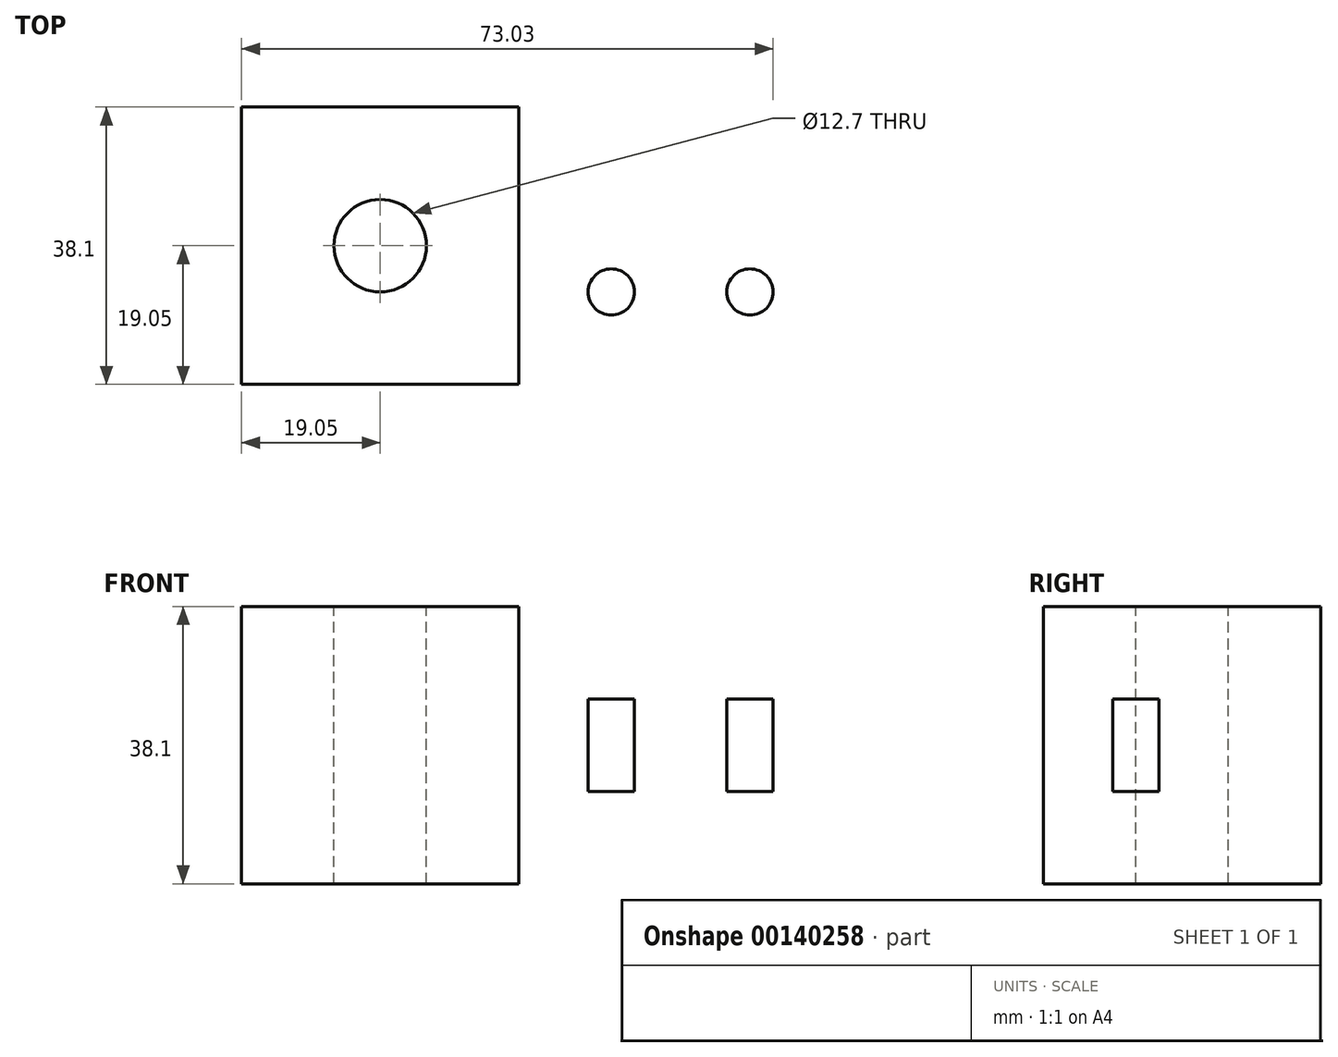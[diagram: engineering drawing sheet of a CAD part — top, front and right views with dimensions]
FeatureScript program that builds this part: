
annotation { "Feature Type Name" : "Feature", "Feature Type Description" : "" }
export const myFeature = defineFeature(function(context is Context, id is Id, definition is map)
    precondition{}
    {
        {
            var Q0;
            Q0=qCreatedBy(makeId("Front.planeOp"),FACE);
            var sketch = newSketch(context, id + "F0", { "sketchPlane" : qUnion([Q0])});
            skLineSegment(sketch, "E0", {"start": v(0, 0) * mm, "end": v(0, 38.1) * mm});
            skLineSegment(sketch, "E1", {"start": v(0, 38.1) * mm, "end": v(38.1, 38.1) * mm});
            skLineSegment(sketch, "E2", {"start": v(38.1, 38.1) * mm, "end": v(38.1, 25.4) * mm});
            skLineSegment(sketch, "E3", {"start": v(38.1, 25.4) * mm, "end": v(88.9, 25.4) * mm});
            skLineSegment(sketch, "E4", {"start": v(88.9, 25.4) * mm, "end": v(88.9, 12.7) * mm});
            skLineSegment(sketch, "E5", {"start": v(88.9, 12.7) * mm, "end": v(38.1, 12.7) * mm});
            skLineSegment(sketch, "E6", {"start": v(38.1, 12.7) * mm, "end": v(38.1, 0) * mm});
            skLineSegment(sketch, "E7", {"start": v(38.1, 0) * mm, "end": v(0, 0) * mm});
            skSolve(sketch);
        }
        {
            var Q0;
            Q0 = qSketchRegion(id + "F0", true);
            extrude(context, id + "F1", {"entities" : qUnion([Q0]), "endBound" : BoundingType.SYMMETRIC, "depth" : 38.1 * mm});
        }
        {
            var Q0;
            Q0=makeQuery(id+"F1.opExtrude","CAP_EDGE",EDGE,{"disambiguationData":[OSD([sQuery(id+"F0.wireOp",EDGE,"E4")])],"isStart":true});
            var Q1;
            Q1=makeQuery(id+"F1.opExtrude","CAP_EDGE",EDGE,{"disambiguationData":[OSD([sQuery(id+"F0.wireOp",EDGE,"E4")])],"isStart":false});
            fillet(context, id + "F2", {"entities" : qUnion([Q0, Q1]), "radius" : 19.05 * mm, "tangentPropagation" : true, "allowEdgeOverflow" : false});
        }
        {
            var Q0;
            Q0=makeQuery(id+"F1.opExtrude","SWEPT_FACE",FACE,{"disambiguationData":[OSD([sQuery(id+"F0.wireOp",EDGE,"E1")])]});
            var sketch = newSketch(context, id + "F3", { "sketchPlane" : qUnion([Q0])});
            skCircle(sketch, "E8", {"center": v(19.05, 0) * mm, "radius": 6.35 * mm});
            skPoint(sketch, "E8.centerSnap0", {"position": v(19.05, 19.05) * mm});
            skSolve(sketch);
        }
        {
            var Q0;
            Q0=makeQuery(id+"F1.opExtrude","SWEPT_FACE",FACE,{"disambiguationData":[OSD([sQuery(id+"F0.wireOp",EDGE,"E3")])]});
            var sketch = newSketch(context, id + "F4", { "sketchPlane" : qUnion([Q0])});
            skCircle(sketch, "E9", {"center": v(50.8, 6.35) * mm, "radius": 3.18 * mm});
            skCircle(sketch, "E10.MirrorC", {"center": v(50.8, -6.35) * mm, "radius": 3.18 * mm});
            skCircle(sketch, "E11", {"center": v(69.85, 6.35) * mm, "radius": 3.18 * mm});
            skCircle(sketch, "E12.MirrorC", {"center": v(69.85, -6.35) * mm, "radius": 3.18 * mm});
            skSolve(sketch);
        }
        {
            var Q0;
            Q0=makeQuery(id+"F3.imprint","IMPRINT",FACE,{"disambiguationData":[TD([[makeQuery(id+"F3.imprint","IMPRINT",EDGE,{"derivedFrom":sQuery(id+"F3.wireOp",EDGE,"E8")}),1.0]])]});
            var Q1;
            Q1=makeQuery(id+"F4.imprint","IMPRINT",FACE,{"disambiguationData":[TD([[makeQuery(id+"F4.imprint","IMPRINT",EDGE,{"derivedFrom":sQuery(id+"F4.wireOp",EDGE,"E9")}),1.0]])]});
            var Q2;
            Q2=makeQuery(id+"F4.imprint","IMPRINT",FACE,{"disambiguationData":[TD([[makeQuery(id+"F4.imprint","IMPRINT",EDGE,{"derivedFrom":sQuery(id+"F4.wireOp",EDGE,"E11")}),1.0]])]});
            var Q3;
            Q3=makeQuery(id+"F4.imprint","IMPRINT",FACE,{"disambiguationData":[TD([[makeQuery(id+"F4.imprint","IMPRINT",EDGE,{"derivedFrom":sQuery(id+"F4.wireOp",EDGE,"E12.MirrorC")}),-1.0]])]});
            var Q4;
            Q4=makeQuery(id+"F4.imprint","IMPRINT",FACE,{"disambiguationData":[TD([[makeQuery(id+"F4.imprint","IMPRINT",EDGE,{"derivedFrom":sQuery(id+"F4.wireOp",EDGE,"E10.MirrorC")}),-1.0]])]});
            extrude(context, id + "F5", {"entities" : qUnion([Q0, Q1, Q2, Q3, Q4]), "operationType" : NewBodyOperationType.REMOVE, "endBound" : BoundingType.THROUGH_ALL, "oppositeDirection" : true, "depth" : 25.4 * mm});
        }
    });
